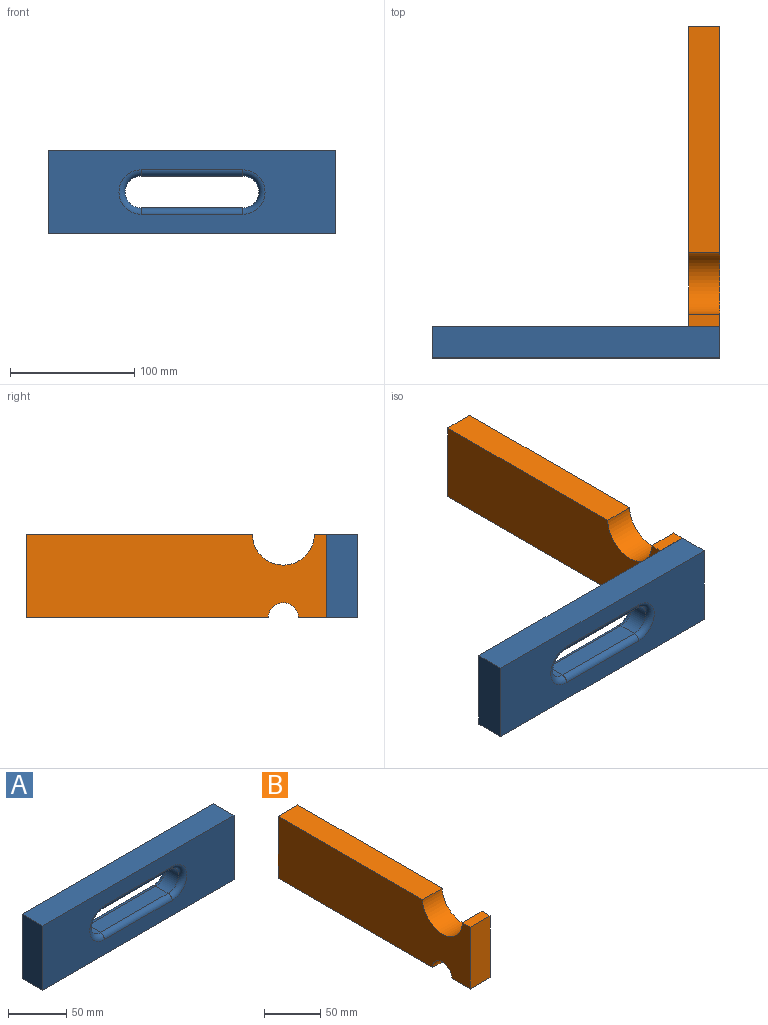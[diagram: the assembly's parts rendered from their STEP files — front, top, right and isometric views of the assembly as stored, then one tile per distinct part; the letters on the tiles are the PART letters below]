
ASSEMBLY  parts=2 mates=1
PART A: 18 faces, bbox 231.6x25x67.5 mm
  f0: plane 231.62x25mm, normal (0,0,1), area 5790.4mm2, adj f1,f7,f8,f9
  f1: plane 67.47x25mm, normal (-1,0,0), area 1686.7mm2, adj f0,f2,f8,f9
  f2: plane 231.62x25mm, normal (0,0,-1), area 5790.4mm2, adj f1,f7,f8,f9
  f3: cylinder r=12.83mm len=25.66mm, axis (0,1,0), area 604.5mm2, adj f4,f6,f11,f15
  f4: plane 81.96x15mm, normal (0,0,-1), area 1229.4mm2, adj f3,f5,f13,f17
  f5: cylinder r=12.83mm len=25.66mm, axis (0,1,0), area 604.5mm2, adj f4,f6,f12,f16
  f6: plane 81.96x15mm, normal (0,0,1), area 1229.4mm2, adj f3,f5,f10,f14
  f7: plane 67.47x25mm, normal (1,0,0), area 1686.7mm2, adj f0,f2,f8,f9
  f8: plane 231.62x67.47mm, normal (0,-1,0), area 11705.5mm2, adj f0,f1,f2,f7,f14,f15,f16,f17
  f9: plane 231.62x67.47mm, normal (0,1,0), area 11705.5mm2, adj f0,f1,f2,f7,f10,f11,f12,f13
  f10: cylinder r=5mm len=81.96mm, axis (-1,0,0), area 643.7mm2, adj f6,f9,f11,f12
  f11: torus R=17.83mm, axis (0,-1,0), area 361.3mm2, adj f3,f9,f10,f13
  f12: torus R=17.83mm, axis (0,-1,0), area 361.3mm2, adj f5,f9,f10,f13
  f13: cylinder r=5mm len=81.96mm, axis (1,0,0), area 643.7mm2, adj f4,f9,f11,f12
  f14: cylinder r=5mm len=81.96mm, axis (1,0,0), area 643.7mm2, adj f6,f8,f15,f16
  f15: torus R=17.83mm, axis (0,-1,0), area 361.3mm2, adj f3,f8,f14,f17
  f16: torus R=17.83mm, axis (0,-1,0), area 361.3mm2, adj f5,f8,f14,f17
  f17: cylinder r=5mm len=81.96mm, axis (-1,0,0), area 643.7mm2, adj f4,f8,f15,f16
PART B: 10 faces, bbox 25x242.1x67.5 mm
  f0: cylinder r=24.99mm len=49.97mm, axis (-1,0,0), area 1962.3mm2, adj f1,f7,f8,f9
  f1: plane 25x10.02mm, normal (0,0,1), area 250.4mm2, adj f0,f2,f8,f9
  f2: plane 67.47x25mm, normal (0,-1,0), area 1686.7mm2, adj f1,f3,f8,f9
  f3: plane 25x22.82mm, normal (0,0,-1), area 570.4mm2, adj f2,f4,f8,f9
  f4: cylinder r=12.18mm len=25mm, axis (-1,0,0), area 956.8mm2, adj f3,f5,f8,f9
  f5: plane 194.89x25mm, normal (0,0,-1), area 4872.2mm2, adj f4,f6,f8,f9
  f6: plane 67.47x25mm, normal (0,1,0), area 1686.7mm2, adj f5,f7,f8,f9
  f7: plane 182.09x25mm, normal (0,0,1), area 4552.1mm2, adj f0,f6,f8,f9
  f8: plane 242.07x67.47mm, normal (1,0,0), area 15117.8mm2, adj f0,f1,f2,f3,f4,f5,f6,f7
  f9: plane 242.07x67.47mm, normal (-1,0,0), area 15117.8mm2, adj f0,f1,f2,f3,f4,f5,f6,f7
PLACE A t=(-66.7,-41.68,-14.07)mm
PLACE B t=(24.13,79.36,-14.04)mm
MATE planar B.f2 <-> A.f9  axis (0,-1,0) through (36.63,-41.68,-14.04)mm
